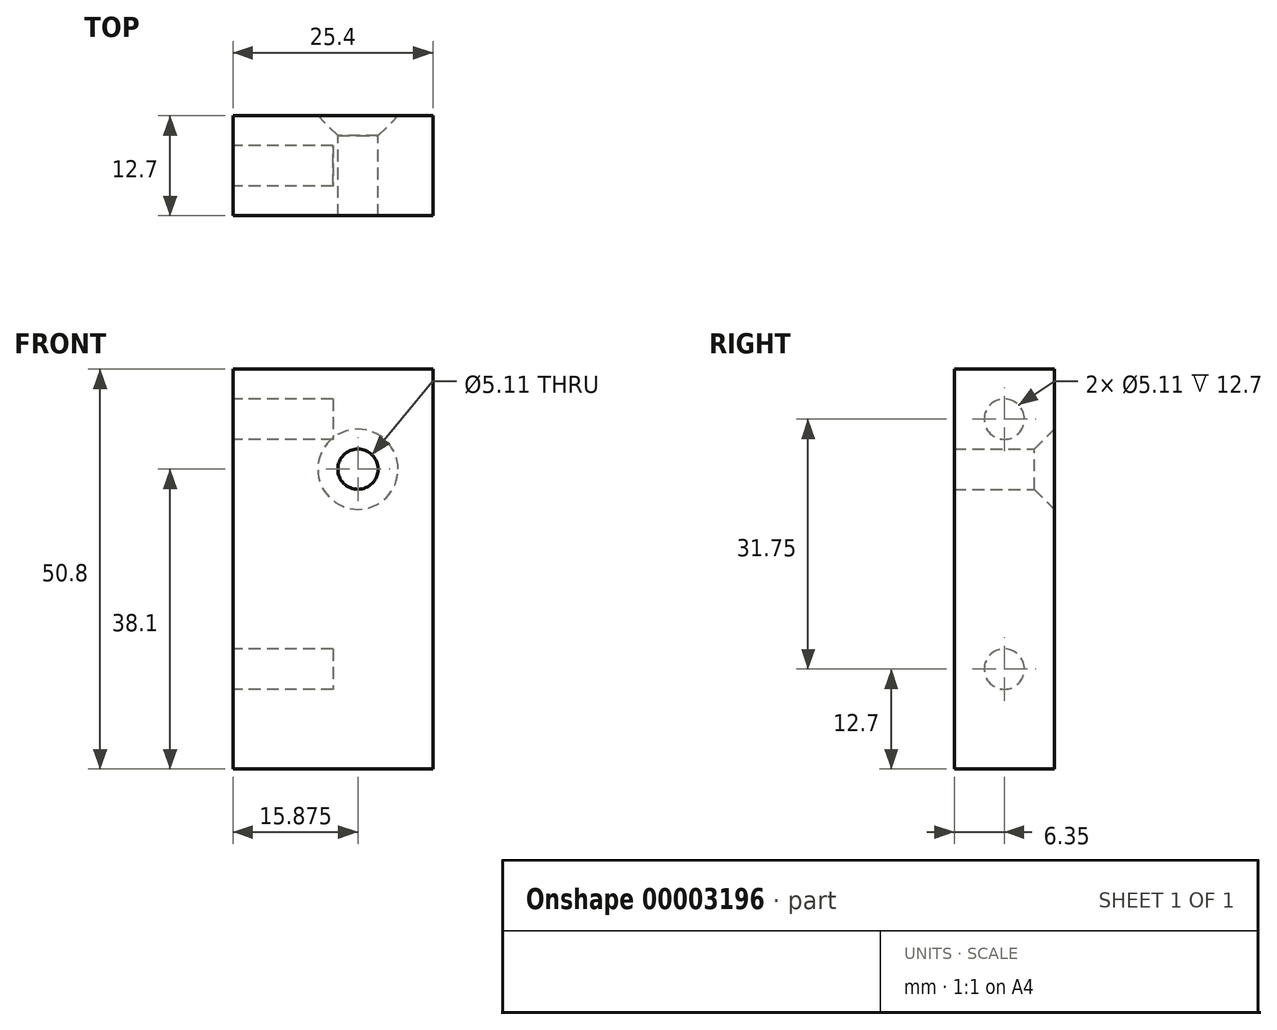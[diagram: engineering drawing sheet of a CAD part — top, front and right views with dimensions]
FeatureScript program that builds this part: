
annotation { "Feature Type Name" : "Feature", "Feature Type Description" : "" }
export const myFeature = defineFeature(function(context is Context, id is Id, definition is map)
    precondition{}
    {
        {
            var Q0;
            Q0=qCreatedBy(makeId("Front.planeOp"),FACE);
            var sketch = newSketch(context, id + "F0", { "sketchPlane" : qUnion([Q0])});
            skLineSegment(sketch, "E0", {"start": v(0, 0) * mm, "end": v(0, -50.8) * mm});
            skLineSegment(sketch, "E1", {"start": v(0, -50.8) * mm, "end": v(25.4, -50.8) * mm});
            skLineSegment(sketch, "E2", {"start": v(25.4, -50.8) * mm, "end": v(25.4, 0) * mm});
            skLineSegment(sketch, "E3", {"start": v(25.4, 0) * mm, "end": v(0, 0) * mm});
            skLineSegment(sketch, "E4", {"start": v(15.88, 0) * mm, "end": v(15.88, -50.8) * mm, "construction": true});
            skLineSegment(sketch, "E5", {"start": v(0, -12.7) * mm, "end": v(25.4, -12.7) * mm, "construction": true});
            skCircle(sketch, "E6", {"center": v(15.88, -12.7) * mm, "radius": 2.55 * mm});
            skSolve(sketch);
        }
        {
            var Q0;
            Q0=makeQuery(id+"F0.imprint","IMPRINT",FACE,{"disambiguationData":[TD([[makeQuery(id+"F0.imprint","IMPRINT",EDGE,{"derivedFrom":sQuery(id+"F0.wireOp",EDGE,"E0")}),1.0]])]});
            extrude(context, id + "F1", {"entities" : qUnion([Q0]), "endBound" : BoundingType.SYMMETRIC, "depth" : 12.7 * mm});
        }
        {
            var Q0;
            Q0=makeQuery(id+"F1.opExtrude","SWEPT_FACE",FACE,{"disambiguationData":[OSD([sQuery(id+"F0.wireOp",EDGE,"E0")])]});
            var sketch = newSketch(context, id + "F2", { "sketchPlane" : qUnion([Q0])});
            skLineSegment(sketch, "E7", {"start": v(0, 0) * mm, "end": v(0, -50.8) * mm, "construction": true});
            skLineSegment(sketch, "E8", {"start": v(-6.35, -6.35) * mm, "end": v(6.35, -6.35) * mm, "construction": true});
            skLineSegment(sketch, "E9", {"start": v(-6.35, -38.1) * mm, "end": v(6.35, -38.1) * mm});
            skCircle(sketch, "E10", {"center": v(0, -6.35) * mm, "radius": 2.55 * mm});
            skCircle(sketch, "E11", {"center": v(0, -38.1) * mm, "radius": 2.55 * mm});
            skSolve(sketch);
        }
        {
            var Q0;
            Q0=makeQuery(id+"F2.imprint","IMPRINT",FACE,{"disambiguationData":[TD([[makeQuery(id+"F2.imprint","IMPRINT",EDGE,{"derivedFrom":sQuery(id+"F2.wireOp",EDGE,"E10")}),1.0]])]});
            var Q1;
            {var subQ0=sQuery(id+"F2.wireOp",EDGE,"E11");var subQ1=sQuery(id+"F2.wireOp",EDGE,"E9");var subQ3=makeQuery(id+"F2.imprint","INTERSECT",VERTEX,{"disambiguationData":[OD(0.0)],"derivedFrom":[subQ1,subQ0]});Q1=makeQuery(id+"F2.imprint","IMPRINT",FACE,{"disambiguationData":[TD([[makeQuery(id+"F2.imprint","IMPRINT",EDGE,{"disambiguationData":[TD([[subQ3,-1.0]])],"derivedFrom":subQ1}),1.0]])]});}
            var Q2;
            {var subQ0=sQuery(id+"F2.wireOp",EDGE,"E11");var subQ1=sQuery(id+"F2.wireOp",EDGE,"E9");var subQ3=makeQuery(id+"F2.imprint","INTERSECT",VERTEX,{"disambiguationData":[OD(0.0)],"derivedFrom":[subQ1,subQ0]});Q2=makeQuery(id+"F2.imprint","IMPRINT",FACE,{"disambiguationData":[TD([[makeQuery(id+"F2.imprint","IMPRINT",EDGE,{"disambiguationData":[TD([[subQ3,-1.0]])],"derivedFrom":subQ1}),-1.0]])]});}
            extrude(context, id + "F3", {"entities" : qUnion([Q0, Q1, Q2]), "operationType" : NewBodyOperationType.REMOVE, "oppositeDirection" : true, "depth" : 12.7 * mm});
        }
        {
            var Q0;
            Q0=makeQuery(id+"F1.opExtrude","CAP_EDGE",EDGE,{"disambiguationData":[OSD([sQuery(id+"F0.wireOp",EDGE,"E6")])],"isStart":true});
            chamfer(context, id + "F4", {"entities" : qUnion([Q0]), "chamferType" : ChamferType.OFFSET_ANGLE, "width" : 2.54 * mm, "oppositeDirection" : false, "angle" : 45 * degree, "tangentPropagation" : true});
        }
    });
